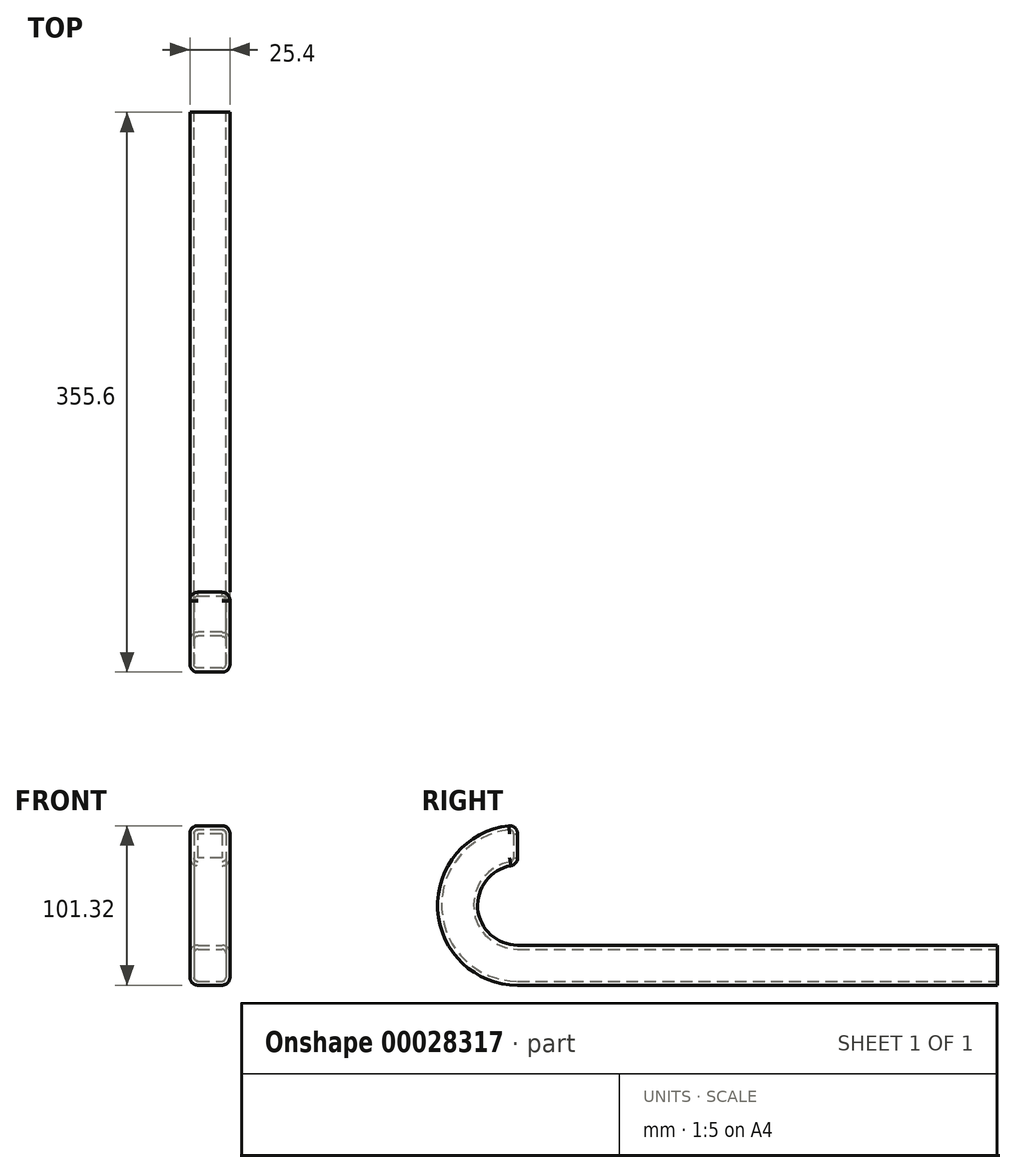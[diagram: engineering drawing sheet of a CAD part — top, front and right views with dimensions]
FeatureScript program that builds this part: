
annotation { "Feature Type Name" : "Feature", "Feature Type Description" : "" }
export const myFeature = defineFeature(function(context is Context, id is Id, definition is map)
    precondition{}
    {
        {
            var Q0;
            Q0=qCreatedBy(makeId("Front.planeOp"),FACE);
            var sketch = newSketch(context, id + "F0", { "sketchPlane" : qUnion([Q0])});
            skLineSegment(sketch, "E0.rect.bottom", {"start": v(-12.7, 12.7) * mm, "end": v(12.7, 12.7) * mm});
            skLineSegment(sketch, "E0.rect.top", {"start": v(-12.7, -12.7) * mm, "end": v(12.7, -12.7) * mm});
            skLineSegment(sketch, "E0.rect.left", {"start": v(-12.7, 12.7) * mm, "end": v(-12.7, -12.7) * mm});
            skLineSegment(sketch, "E0.rect.right", {"start": v(12.7, 12.7) * mm, "end": v(12.7, -12.7) * mm});
            skPoint(sketch, "E0.rect.middle", {"position": v(0, 0) * mm});
            skSolve(sketch);
        }
        {
            var Q0;
            Q0 = qSketchRegion(id + "F0", true);
            extrude(context, id + "F1", {"entities" : qUnion([Q0]), "depth" : 304.8 * mm});
        }
        {
            var Q0;
            Q0=makeQuery(id+"F1.opExtrude","SWEPT_FACE",FACE,{"disambiguationData":[OSD([sQuery(id+"F0.wireOp",EDGE,"E0.rect.right")])]});
            var sketch = newSketch(context, id + "F2", { "sketchPlane" : qUnion([Q0])});
            skArc(sketch, "E1", {"start": v(-304.8, 63.5) * mm, "mid": v(-330.2, 38.1) * mm, "end": v(-304.8, 12.7) * mm});
            skSolve(sketch);
        }
        {
            var Q0;
            Q0=makeQuery(id+"F1.opExtrude","CAP_FACE",FACE,{"disambiguationData":[OSD([sQuery(id+"F0.wireOp",EDGE,"E0.rect.bottom"),sQuery(id+"F0.wireOp",EDGE,"E0.rect.top"),sQuery(id+"F0.wireOp",EDGE,"E0.rect.left"),sQuery(id+"F0.wireOp",EDGE,"E0.rect.right")])],"isStart":false});
            var Q1;
            Q1=sQuery(id+"F2.wireOp",EDGE,"E1");
            sweep(context, id + "F3", {"operationType" : NewBodyOperationType.ADD, "profiles" : qUnion([Q0]), "path" : qUnion([Q1])});
        }
        {
            var Q0;
            Q0=makeQuery(id+"F3.opSweep","SWEPT_EDGE",EDGE,{"disambiguationData":[OSD([sQuery(id+"F0.wireOp",EDGE,"E0.rect.bottom"),sQuery(id+"F0.wireOp",EDGE,"E0.rect.right"),sQuery(id+"F2.wireOp",EDGE,"E1")])]});
            var Q1;
            Q1=makeQuery(id+"F3.opSweep","SWEPT_EDGE",EDGE,{"disambiguationData":[OSD([sQuery(id+"F0.wireOp",EDGE,"E0.rect.bottom"),sQuery(id+"F0.wireOp",EDGE,"E0.rect.left"),sQuery(id+"F2.wireOp",EDGE,"E1")])]});
            var Q2;
            Q2=makeQuery(id+"F3.opSweep","CAP_EDGE",EDGE,{"disambiguationData":[OSD([sQuery(id+"F0.wireOp",EDGE,"E0.rect.bottom"),sQuery(id+"F2.wireOp",VERTEX,"E1.start")])],"isStart":false});
            var Q3;
            {var subQ0=sQuery(id+"F0.wireOp",EDGE,"E0.rect.bottom");Q3=makeQuery(id+"F3.boolean.opBoolean","MERGE",EDGE,{"derivedFrom":[makeQuery(id+"F1.opExtrude","CAP_EDGE",EDGE,{"disambiguationData":[OSD([subQ0])],"isStart":false}),makeQuery(id+"F3.opSweep","CAP_EDGE",EDGE,{"disambiguationData":[OSD([subQ0,sQuery(id+"F2.wireOp",VERTEX,"E1.end")])],"isStart":true})]});}
            fillet(context, id + "F4", {"entities" : qUnion([Q0, Q1, Q2, Q3]), "radius" : 5.08 * mm, "tangentPropagation" : true, "allowEdgeOverflow" : false});
        }
        {
            var Q0;
            Q0=makeQuery(id+"F3.opSweep","CAP_EDGE",EDGE,{"disambiguationData":[OSD([sQuery(id+"F0.wireOp",EDGE,"E0.rect.right"),sQuery(id+"F2.wireOp",VERTEX,"E1.start")])],"isStart":false});
            var Q1;
            Q1=makeQuery(id+"F3.opSweep","CAP_EDGE",EDGE,{"disambiguationData":[OSD([sQuery(id+"F0.wireOp",EDGE,"E0.rect.top"),sQuery(id+"F2.wireOp",VERTEX,"E1.start")])],"isStart":false});
            var Q2;
            Q2=makeQuery(id+"F3.opSweep","CAP_EDGE",EDGE,{"disambiguationData":[OSD([sQuery(id+"F0.wireOp",EDGE,"E0.rect.left"),sQuery(id+"F2.wireOp",VERTEX,"E1.start")])],"isStart":false});
            fillet(context, id + "F5", {"entities" : qUnion([Q0, Q1, Q2]), "radius" : 5.08 * mm, "tangentPropagation" : true, "allowEdgeOverflow" : false});
        }
        {
            var Q0;
            Q0=makeQuery(id+"F3.opSweep","SWEPT_EDGE",EDGE,{"disambiguationData":[OSD([sQuery(id+"F0.wireOp",EDGE,"E0.rect.top"),sQuery(id+"F0.wireOp",EDGE,"E0.rect.right"),sQuery(id+"F2.wireOp",EDGE,"E1")])]});
            var Q1;
            Q1=makeQuery(id+"F3.opSweep","SWEPT_EDGE",EDGE,{"disambiguationData":[OSD([sQuery(id+"F0.wireOp",EDGE,"E0.rect.top"),sQuery(id+"F0.wireOp",EDGE,"E0.rect.left"),sQuery(id+"F2.wireOp",EDGE,"E1")])]});
            fillet(context, id + "F6", {"entities" : qUnion([Q0, Q1]), "radius" : 5.08 * mm, "tangentPropagation" : true, "allowEdgeOverflow" : false});
        }
        {
            var Q0;
            Q0=makeQuery(id+"F1.opExtrude","CAP_FACE",FACE,{"disambiguationData":[OSD([sQuery(id+"F0.wireOp",EDGE,"E0.rect.bottom"),sQuery(id+"F0.wireOp",EDGE,"E0.rect.top"),sQuery(id+"F0.wireOp",EDGE,"E0.rect.left"),sQuery(id+"F0.wireOp",EDGE,"E0.rect.right")])],"isStart":true});
            shell(context, id + "F7", {"entities" : qUnion([Q0]), "thickness" : 2.54 * mm});
        }
        {
            var Q0;
            Q0=makeQuery(id+"F3.opSweep","CAP_FACE",FACE,{"disambiguationData":[OSD([sQuery(id+"F0.wireOp",EDGE,"E0.rect.bottom"),sQuery(id+"F0.wireOp",EDGE,"E0.rect.top"),sQuery(id+"F0.wireOp",EDGE,"E0.rect.left"),sQuery(id+"F0.wireOp",EDGE,"E0.rect.right"),sQuery(id+"F2.wireOp",VERTEX,"E1.start")])],"isStart":false});
            var sketch = newSketch(context, id + "F8", { "sketchPlane" : qUnion([Q0])});
            skLineSegment(sketch, "E2.bottom", {"start": v(7.62, 83.54) * mm, "end": v(-7.62, 83.54) * mm});
            skLineSegment(sketch, "E2.top", {"start": v(7.62, 68.15) * mm, "end": v(-7.62, 68.15) * mm});
            skLineSegment(sketch, "E2.left", {"start": v(7.62, 83.54) * mm, "end": v(7.62, 68.15) * mm});
            skLineSegment(sketch, "E2.right", {"start": v(-7.62, 83.54) * mm, "end": v(-7.62, 68.15) * mm});
            skSolve(sketch);
        }
        {
            var Q0;
            Q0 = qSketchRegion(id + "F8", true);
            extrude(context, id + "F9", {"entities" : qUnion([Q0]), "operationType" : NewBodyOperationType.REMOVE, "oppositeDirection" : true, "depth" : 12.7 * mm});
        }
    });
